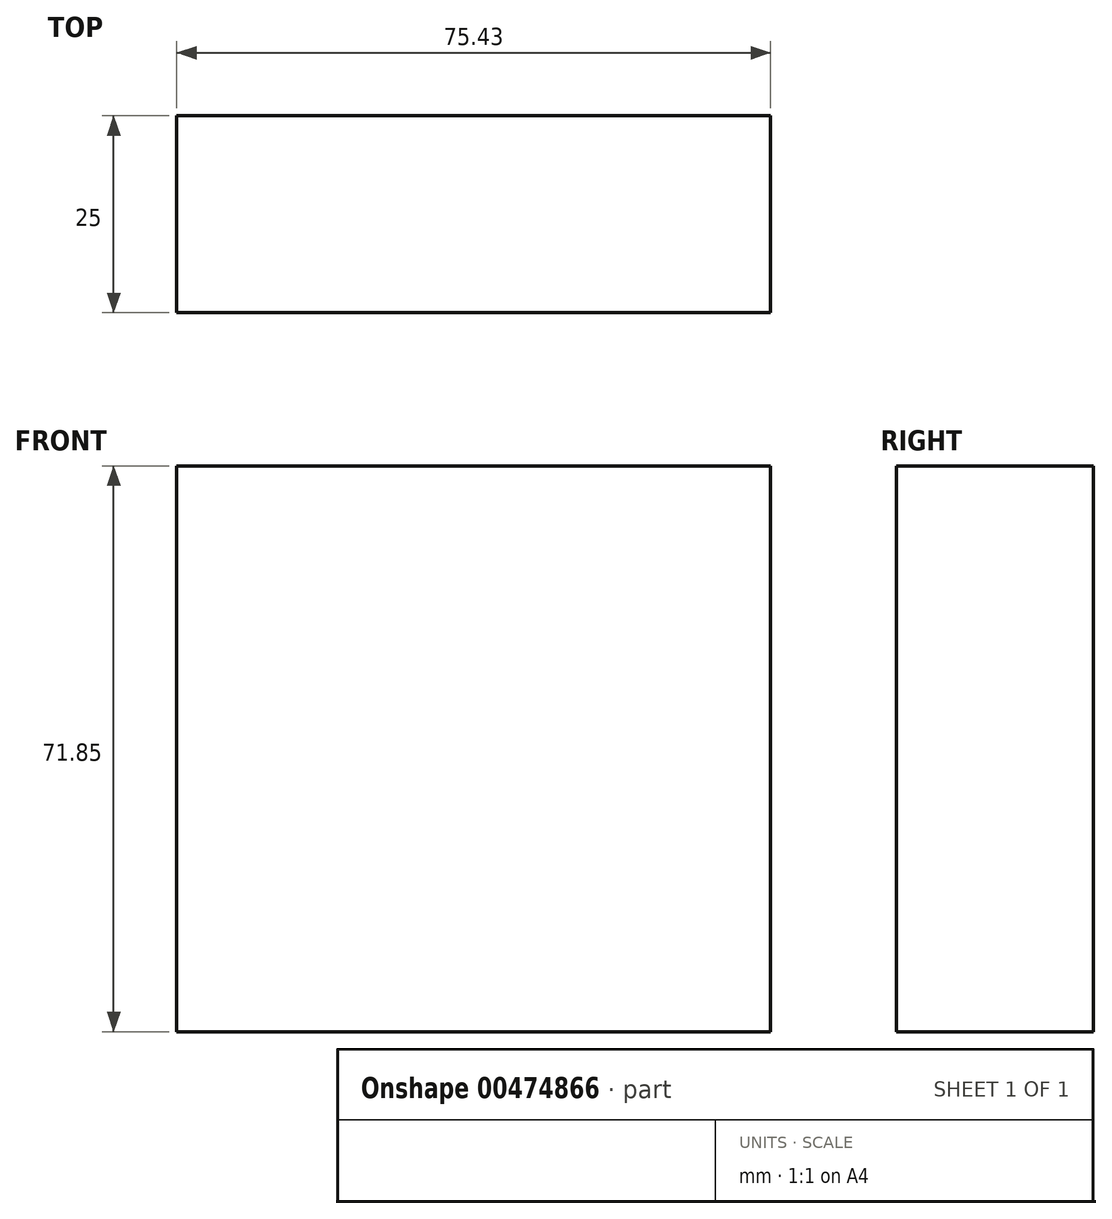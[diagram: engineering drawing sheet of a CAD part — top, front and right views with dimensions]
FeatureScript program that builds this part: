
annotation { "Feature Type Name" : "Feature", "Feature Type Description" : "" }
export const myFeature = defineFeature(function(context is Context, id is Id, definition is map)
    precondition{}
    {
        {
            var Q0;
            Q0=qCreatedBy(makeId("Front.planeOp"),FACE);
            var sketch = newSketch(context, id + "F0", { "sketchPlane" : qUnion([Q0])});
            skLineSegment(sketch, "E0.bottom", {"start": v(-92.8, 11.93) * mm, "end": v(-17.36, 11.93) * mm});
            skLineSegment(sketch, "E0.top", {"start": v(-92.8, 83.78) * mm, "end": v(-17.36, 83.78) * mm});
            skLineSegment(sketch, "E0.left", {"start": v(-92.8, 11.93) * mm, "end": v(-92.8, 83.78) * mm});
            skLineSegment(sketch, "E0.right", {"start": v(-17.36, 11.93) * mm, "end": v(-17.36, 83.78) * mm});
            skPoint(sketch, "E0.middle", {"position": v(-55.07, 47.85) * mm});
            skSolve(sketch);
        }
        {
            var Q0;
            Q0=makeQuery(id+"F0.imprint","IMPRINT",FACE,{"disambiguationData":[TD([[makeQuery(id+"F0.imprint","IMPRINT",EDGE,{"derivedFrom":sQuery(id+"F0.wireOp",EDGE,"E0.bottom")}),1.0]])]});
            extrude(context, id + "F1", {"entities" : qUnion([Q0]), "depth" : 25 * mm});
        }
    });
